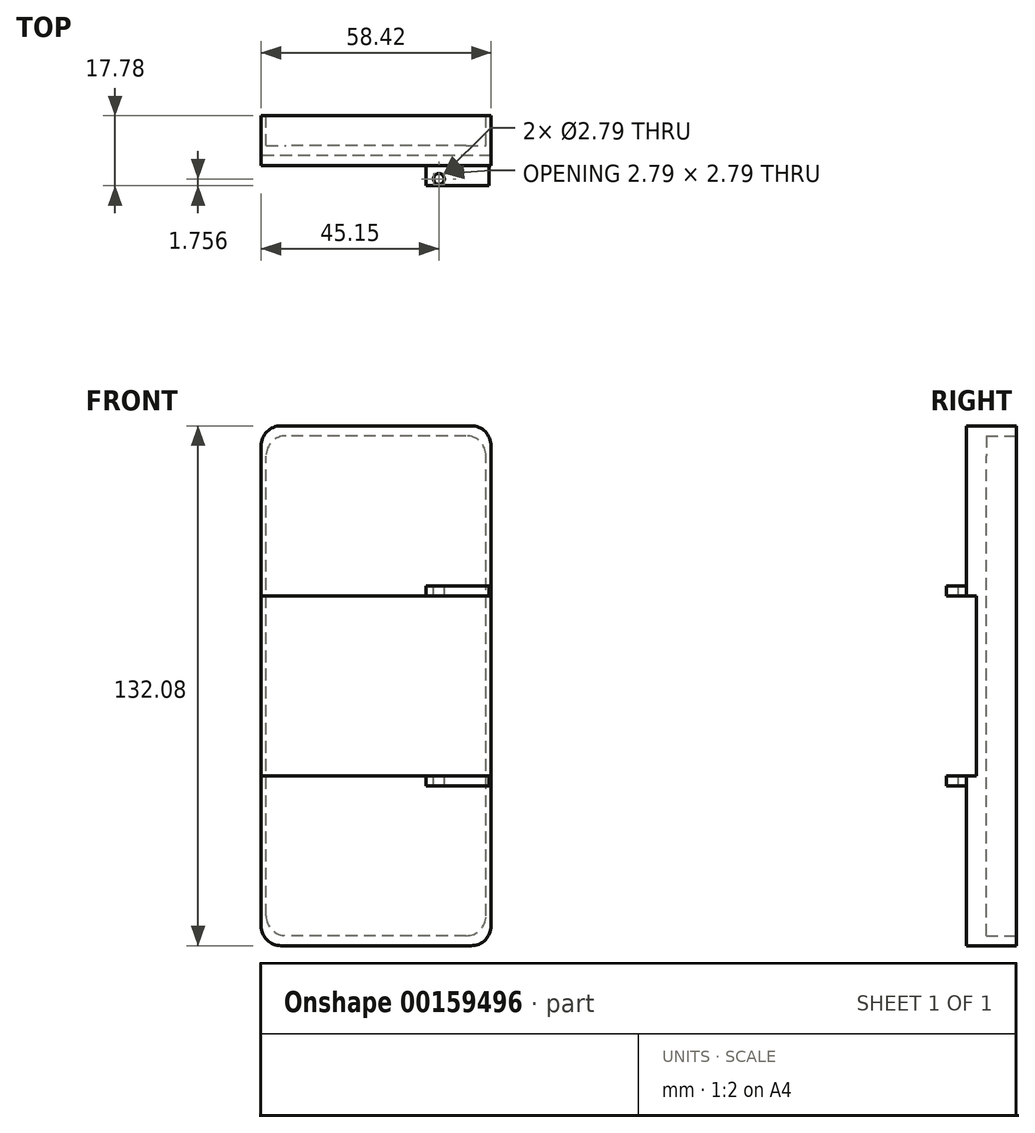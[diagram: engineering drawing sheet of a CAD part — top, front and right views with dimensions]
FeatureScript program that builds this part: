
annotation { "Feature Type Name" : "Feature", "Feature Type Description" : "" }
export const myFeature = defineFeature(function(context is Context, id is Id, definition is map)
    precondition{}
    {
        {
            var Q0;
            Q0=qCreatedBy(makeId("Front.planeOp"),FACE);
            var sketch = newSketch(context, id + "F0", { "sketchPlane" : qUnion([Q0])});
            skLineSegment(sketch, "E0.bottom", {"start": v(-29.2, -66.04) * mm, "end": v(29.21, -66.04) * mm});
            skLineSegment(sketch, "E0.top", {"start": v(-29.21, 66.04) * mm, "end": v(29.21, 66.04) * mm});
            skLineSegment(sketch, "E0.left", {"start": v(-29.2, -66.04) * mm, "end": v(-29.21, 66.04) * mm});
            skLineSegment(sketch, "E0.right", {"start": v(29.21, -66.04) * mm, "end": v(29.2, 66.04) * mm});
            skPoint(sketch, "E0.middle", {"position": v(0, 0) * mm});
            skSolve(sketch);
        }
        {
            var Q0;
            Q0 = qSketchRegion(id + "F0", true);
            extrude(context, id + "F1", {"entities" : qUnion([Q0]), "depth" : 12.7 * mm});
        }
        {
            var Q0;
            Q0=makeQuery(id+"F1.opExtrude","SWEPT_EDGE",EDGE,{"disambiguationData":[OSD([sQuery(id+"F0.wireOp",EDGE,"E0.top"),sQuery(id+"F0.wireOp",EDGE,"E0.left")])]});
            var Q1;
            Q1=makeQuery(id+"F1.opExtrude","SWEPT_EDGE",EDGE,{"disambiguationData":[OSD([sQuery(id+"F0.wireOp",EDGE,"E0.top"),sQuery(id+"F0.wireOp",EDGE,"E0.right")])]});
            var Q2;
            Q2=makeQuery(id+"F1.opExtrude","SWEPT_EDGE",EDGE,{"disambiguationData":[OSD([sQuery(id+"F0.wireOp",EDGE,"E0.bottom"),sQuery(id+"F0.wireOp",EDGE,"E0.right")])]});
            var Q3;
            Q3=makeQuery(id+"F1.opExtrude","SWEPT_EDGE",EDGE,{"disambiguationData":[OSD([sQuery(id+"F0.wireOp",EDGE,"E0.bottom"),sQuery(id+"F0.wireOp",EDGE,"E0.left")])]});
            fillet(context, id + "F2", {"entities" : qUnion([Q0, Q1, Q2, Q3]), "radius" : 5.08 * mm, "tangentPropagation" : true, "allowEdgeOverflow" : false});
        }
        {
            var Q0;
            Q0=qCreatedBy(makeId("Front.planeOp"),FACE);
            var sketch = newSketch(context, id + "F3", { "sketchPlane" : qUnion([Q0])});
            skLineSegment(sketch, "E1.bottom", {"start": v(27.94, -63.5) * mm, "end": v(-27.94, -63.5) * mm});
            skLineSegment(sketch, "E1.top", {"start": v(27.94, 63.5) * mm, "end": v(-27.94, 63.5) * mm});
            skLineSegment(sketch, "E1.left", {"start": v(27.94, -63.5) * mm, "end": v(27.94, 63.5) * mm});
            skLineSegment(sketch, "E1.right", {"start": v(-27.94, -63.5) * mm, "end": v(-27.94, 63.5) * mm});
            skPoint(sketch, "E1.middle", {"position": v(0, 0) * mm});
            skSolve(sketch);
        }
        {
            var Q0;
            Q0 = qSketchRegion(id + "F3", true);
            extrude(context, id + "F4", {"entities" : qUnion([Q0]), "operationType" : NewBodyOperationType.REMOVE, "depth" : 7.62 * mm});
        }
        {
            var Q0;
            Q0=makeQuery(id+"F4.boolean.opBoolean","COPY",EDGE,{"derivedFrom":makeQuery(id+"F4.opExtrude","SWEPT_EDGE",EDGE,{"disambiguationData":[OSD([sQuery(id+"F3.wireOp",EDGE,"E1.top"),sQuery(id+"F3.wireOp",EDGE,"E1.left")])]})});
            var Q1;
            Q1=makeQuery(id+"F4.boolean.opBoolean","COPY",EDGE,{"derivedFrom":makeQuery(id+"F4.opExtrude","SWEPT_EDGE",EDGE,{"disambiguationData":[OSD([sQuery(id+"F3.wireOp",EDGE,"E1.top"),sQuery(id+"F3.wireOp",EDGE,"E1.right")])]})});
            var Q2;
            Q2=makeQuery(id+"F4.boolean.opBoolean","COPY",EDGE,{"derivedFrom":makeQuery(id+"F4.opExtrude","SWEPT_EDGE",EDGE,{"disambiguationData":[OSD([sQuery(id+"F3.wireOp",EDGE,"E1.bottom"),sQuery(id+"F3.wireOp",EDGE,"E1.right")])]})});
            var Q3;
            Q3=makeQuery(id+"F4.boolean.opBoolean","COPY",EDGE,{"derivedFrom":makeQuery(id+"F4.opExtrude","SWEPT_EDGE",EDGE,{"disambiguationData":[OSD([sQuery(id+"F3.wireOp",EDGE,"E1.bottom"),sQuery(id+"F3.wireOp",EDGE,"E1.left")])]})});
            fillet(context, id + "F5", {"entities" : qUnion([Q0, Q1, Q2, Q3]), "radius" : 5.08 * mm, "tangentPropagation" : true, "allowEdgeOverflow" : false});
        }
        {
            var Q0;
            Q0=qCreatedBy(makeId("Front.planeOp"),FACE);
            var sketch = newSketch(context, id + "F6", { "sketchPlane" : qUnion([Q0])});
            skLineSegment(sketch, "E2.bottom", {"start": v(36.83, 22.86) * mm, "end": v(-36.83, 22.86) * mm});
            skLineSegment(sketch, "E2.top", {"start": v(36.83, -22.86) * mm, "end": v(-36.83, -22.86) * mm});
            skLineSegment(sketch, "E2.left", {"start": v(36.83, 22.86) * mm, "end": v(36.83, -22.86) * mm});
            skLineSegment(sketch, "E2.right", {"start": v(-36.83, 22.86) * mm, "end": v(-36.83, -22.86) * mm});
            skPoint(sketch, "E2.middle", {"position": v(0, 0) * mm});
            skSolve(sketch);
        }
        {
            var Q0;
            Q0=makeQuery(id+"F6.imprint","IMPRINT",FACE,{"disambiguationData":[TD([[makeQuery(id+"F6.imprint","IMPRINT",EDGE,{"derivedFrom":sQuery(id+"F6.wireOp",EDGE,"E2.bottom")}),1.0]])]});
            extrude(context, id + "F7", {"entities" : qUnion([Q0]), "operationType" : NewBodyOperationType.REMOVE, "depth" : 25.4 * mm, "hasSecondDirection" : true, "secondDirectionOppositeDirection" : false, "secondDirectionDepth" : 10.16 * mm});
        }
        {
            var Q0;
            Q0=qCreatedBy(makeId("Front.planeOp"),FACE);
            var sketch = newSketch(context, id + "F8", { "sketchPlane" : qUnion([Q0])});
            skLineSegment(sketch, "E3.bottom", {"start": v(28.7, 22.86) * mm, "end": v(12.7, 22.86) * mm});
            skLineSegment(sketch, "E3.top", {"start": v(28.7, 25.4) * mm, "end": v(12.7, 25.4) * mm});
            skLineSegment(sketch, "E3.left", {"start": v(28.7, 22.86) * mm, "end": v(28.7, 25.4) * mm});
            skLineSegment(sketch, "E3.right", {"start": v(12.7, 22.86) * mm, "end": v(12.7, 25.4) * mm});
            skLineSegment(sketch, "E4.bottom", {"start": v(12.7, -22.86) * mm, "end": v(28.7, -22.86) * mm});
            skLineSegment(sketch, "E4.top", {"start": v(12.7, -25.4) * mm, "end": v(28.7, -25.4) * mm});
            skLineSegment(sketch, "E4.left", {"start": v(12.7, -22.86) * mm, "end": v(12.7, -25.4) * mm});
            skLineSegment(sketch, "E4.right", {"start": v(28.7, -22.86) * mm, "end": v(28.7, -25.4) * mm});
            skSolve(sketch);
        }
        {
            var Q0;
            Q0 = qSketchRegion(id + "F8", true);
            extrude(context, id + "F9", {"entities" : qUnion([Q0]), "operationType" : NewBodyOperationType.ADD, "depth" : 17.78 * mm, "hasSecondDirection" : true, "secondDirectionOppositeDirection" : false, "secondDirectionDepth" : 12.57 * mm});
        }
        {
            var Q0;
            Q0=qCreatedBy(makeId("Top.planeOp"),FACE);
            var sketch = newSketch(context, id + "F10", { "sketchPlane" : qUnion([Q0])});
            skCircle(sketch, "E5", {"center": v(15.94, -16.02) * mm, "radius": 1.4 * mm});
            skSolve(sketch);
        }
        {
            var Q0;
            Q0 = qSketchRegion(id + "F10", true);
            extrude(context, id + "F11", {"entities" : qUnion([Q0]), "operationType" : NewBodyOperationType.REMOVE, "oppositeDirection" : true, "depth" : 25.4 * mm, "hasSecondDirection" : true, "secondDirectionOppositeDirection" : false, "secondDirectionDepth" : 25.4 * mm});
        }
        {
            var Q0;
            Q0=qCreatedBy(makeId("Top.planeOp"),FACE);
            var sketch = newSketch(context, id + "F12", { "sketchPlane" : qUnion([Q0])});
            skLineSegment(sketch, "E6.bottom", {"start": v(-6.07, -7.69) * mm, "end": v(6.63, -7.69) * mm});
            skLineSegment(sketch, "E6.top", {"start": v(-6.07, -1.34) * mm, "end": v(6.63, -1.34) * mm});
            skLineSegment(sketch, "E6.left", {"start": v(-6.07, -7.69) * mm, "end": v(-6.07, -1.34) * mm});
            skLineSegment(sketch, "E6.right", {"start": v(6.63, -7.69) * mm, "end": v(6.63, -1.34) * mm});
            skSolve(sketch);
        }
        {
            var Q0;
            Q0 = qSketchRegion(id + "F12", true);
            extrude(context, id + "F13", {"entities" : qUnion([Q0]), "operationType" : NewBodyOperationType.REMOVE, "oppositeDirection" : true, "depth" : 118.36 * mm, "hasSecondDirection" : true, "secondDirectionOppositeDirection" : true, "secondDirectionDepth" : 73.66 * mm});
        }
        {
            var Q0;
            Q0=qCreatedBy(makeId("Top.planeOp"),FACE);
            var sketch = newSketch(context, id + "F14", { "sketchPlane" : qUnion([Q0])});
            skLineSegment(sketch, "E7.bottom", {"start": v(26.69, -7.59) * mm, "end": v(35.58, -7.59) * mm});
            skLineSegment(sketch, "E7.top", {"start": v(26.69, -1.5) * mm, "end": v(35.58, -1.5) * mm});
            skLineSegment(sketch, "E7.left", {"start": v(26.69, -7.59) * mm, "end": v(26.69, -1.5) * mm});
            skLineSegment(sketch, "E7.right", {"start": v(35.58, -7.59) * mm, "end": v(35.58, -1.5) * mm});
            skSolve(sketch);
        }
        {
            var Q0;
            Q0 = qSketchRegion(id + "F14", true);
            extrude(context, id + "F15", {"entities" : qUnion([Q0]), "operationType" : NewBodyOperationType.REMOVE, "oppositeDirection" : true, "depth" : 117.6 * mm, "hasSecondDirection" : true, "secondDirectionOppositeDirection" : true, "secondDirectionDepth" : 75.95 * mm});
        }
        {
            var Q0;
            Q0=qCreatedBy(makeId("Right.planeOp"),FACE);
            var sketch = newSketch(context, id + "F16", { "sketchPlane" : qUnion([Q0])});
            skLineSegment(sketch, "E8.bottom", {"start": v(-2.74, 72.83) * mm, "end": v(-7.82, 72.83) * mm});
            skLineSegment(sketch, "E8.top", {"start": v(-2.74, 65.2) * mm, "end": v(-7.82, 65.2) * mm});
            skLineSegment(sketch, "E8.left", {"start": v(-2.74, 72.83) * mm, "end": v(-2.74, 65.2) * mm});
            skLineSegment(sketch, "E8.right", {"start": v(-7.82, 72.83) * mm, "end": v(-7.82, 65.2) * mm});
            skSolve(sketch);
        }
        {
            var Q0;
            Q0 = qSketchRegion(id + "F16", true);
            extrude(context, id + "F17", {"entities" : qUnion([Q0]), "operationType" : NewBodyOperationType.REMOVE, "depth" : 57.66 * mm, "hasSecondDirection" : true, "secondDirectionOppositeDirection" : false, "secondDirectionDepth" : 39.88 * mm});
        }
        {
            var Q0;
            Q0=qCreatedBy(makeId("Right.planeOp"),FACE);
            var sketch = newSketch(context, id + "F18", { "sketchPlane" : qUnion([Q0])});
            skLineSegment(sketch, "E9.bottom", {"start": v(-6.87, 64.27) * mm, "end": v(-3.82, 64.27) * mm});
            skLineSegment(sketch, "E9.top", {"start": v(-6.87, 38.87) * mm, "end": v(-3.82, 38.87) * mm});
            skLineSegment(sketch, "E9.left", {"start": v(-6.87, 64.27) * mm, "end": v(-6.87, 38.87) * mm});
            skLineSegment(sketch, "E9.right", {"start": v(-3.82, 64.27) * mm, "end": v(-3.82, 38.87) * mm});
            skSolve(sketch);
        }
        {
            var Q0;
            Q0 = qSketchRegion(id + "F18", true);
            extrude(context, id + "F19", {"entities" : qUnion([Q0]), "operationType" : NewBodyOperationType.REMOVE, "depth" : 79.76 * mm, "hasSecondDirection" : true, "secondDirectionOppositeDirection" : false, "secondDirectionDepth" : 33.02 * mm});
        }
    });
